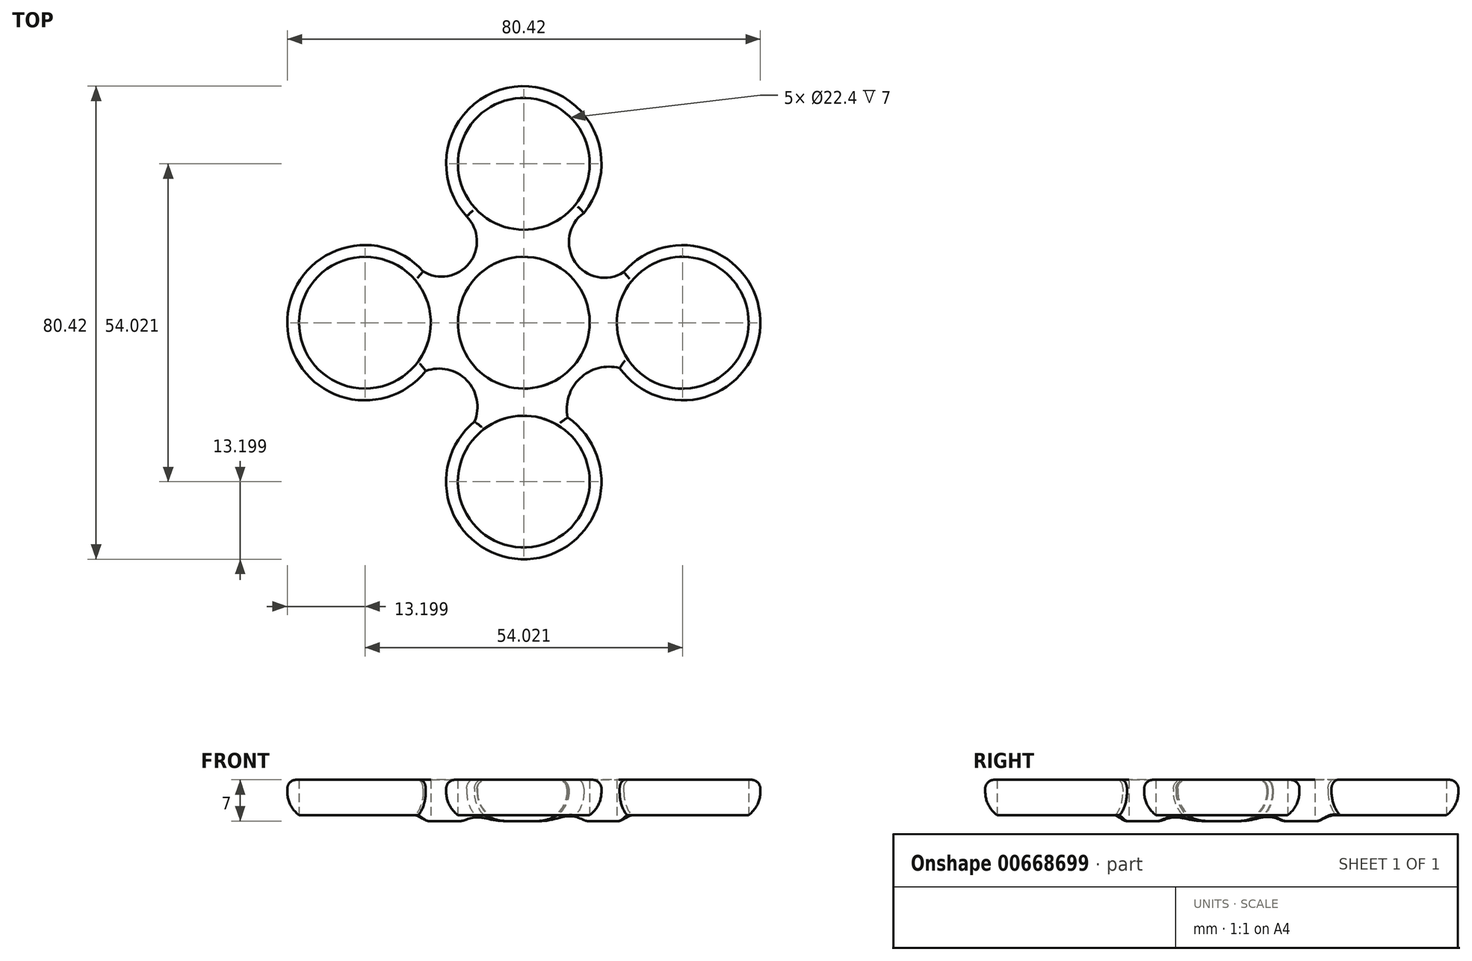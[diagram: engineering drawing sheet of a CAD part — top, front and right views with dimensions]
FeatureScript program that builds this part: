
annotation { "Feature Type Name" : "Feature", "Feature Type Description" : "" }
export const myFeature = defineFeature(function(context is Context, id is Id, definition is map)
    precondition{}
    {
        {
            var Q0;
            Q0=qCreatedBy(makeId("Top.planeOp"),FACE);
            var sketch = newSketch(context, id + "F0", { "sketchPlane" : qUnion([Q0])});
            skCircle(sketch, "E0", {"center": v(0, 0) * mm, "radius": 11.2 * mm});
            skCircle(sketch, "E1", {"center": v(0, 27.01) * mm, "radius": 11.2 * mm});
            skArc(sketch, "E2", {"start": v(8.69, 17.07) * mm, "mid": v(0.57, 40.2) * mm, "end": v(-9.5, 17.85) * mm});
            skCircle(sketch, "E3.1.0", {"center": v(-27.01, 0) * mm, "radius": 11.2 * mm});
            skArc(sketch, "E3.1.1", {"start": v(-17.1, 8.73) * mm, "mid": v(-40.2, -0.34) * mm, "end": v(-16.68, -8.21) * mm});
            skCircle(sketch, "E3.2.0", {"center": v(0, -27.01) * mm, "radius": 11.2 * mm});
            skArc(sketch, "E3.2.1", {"start": v(-8.38, -16.81) * mm, "mid": v(0.58, -40.2) * mm, "end": v(7.46, -16.12) * mm});
            skCircle(sketch, "E3.3.0", {"center": v(27.01, 0) * mm, "radius": 11.2 * mm});
            skArc(sketch, "E3.3.1", {"start": v(16.3, -7.7) * mm, "mid": v(40.2, -0.56) * mm, "end": v(17, 8.6) * mm});
            skArc(sketch, "E4", {"start": v(10.22, 18.65) * mm, "mid": v(8.7, 10.33) * mm, "end": v(17, 8.6) * mm});
            skArc(sketch, "E5", {"start": v(16.3, -7.7) * mm, "mid": v(9.54, -9.46) * mm, "end": v(7.46, -16.12) * mm});
            skArc(sketch, "E6", {"start": v(-8.38, -16.81) * mm, "mid": v(-9.7, -9.79) * mm, "end": v(-16.68, -8.21) * mm});
            skArc(sketch, "E7", {"start": v(-17.1, 8.73) * mm, "mid": v(-9.27, 10.11) * mm, "end": v(-9.7, 18.06) * mm});
            skPoint(sketch, "E7.endSnap0", {"position": v(-9.7, -9.79) * mm});
            skSolve(sketch);
        }
        {
            var Q0;
            Q0=makeQuery(id+"F0.imprint","IMPRINT",FACE,{"disambiguationData":[TD([[makeQuery(id+"F0.imprint","IMPRINT",EDGE,{"derivedFrom":sQuery(id+"F0.wireOp",EDGE,"E0")}),-1.0]])]});
            extrude(context, id + "F1", {"entities" : qUnion([Q0]), "depth" : 7 * mm, "offsetDistance" : 25 * mm});
        }
        {
            var Q0;
            Q0=makeQuery(id+"F1.opExtrude","CAP_EDGE",EDGE,{"disambiguationData":[OSD([sQuery(id+"F0.wireOp",EDGE,"E5")])],"isStart":false});
            var Q1;
            Q1=makeQuery(id+"F1.opExtrude","CAP_EDGE",EDGE,{"disambiguationData":[OSD([sQuery(id+"F0.wireOp",EDGE,"E3.3.1")])],"isStart":false});
            var Q2;
            Q2=makeQuery(id+"F1.opExtrude","CAP_EDGE",EDGE,{"disambiguationData":[OSD([sQuery(id+"F0.wireOp",EDGE,"E4")])],"isStart":false});
            var Q3;
            Q3=makeQuery(id+"F1.opExtrude","CAP_EDGE",EDGE,{"disambiguationData":[OSD([sQuery(id+"F0.wireOp",EDGE,"E2")])],"isStart":false});
            var Q4;
            Q4=makeQuery(id+"F1.opExtrude","CAP_EDGE",EDGE,{"disambiguationData":[OSD([sQuery(id+"F0.wireOp",EDGE,"E7")])],"isStart":false});
            var Q5;
            Q5=makeQuery(id+"F1.opExtrude","CAP_EDGE",EDGE,{"disambiguationData":[OSD([sQuery(id+"F0.wireOp",EDGE,"E3.1.1")])],"isStart":false});
            var Q6;
            Q6=makeQuery(id+"F1.opExtrude","CAP_EDGE",EDGE,{"disambiguationData":[OSD([sQuery(id+"F0.wireOp",EDGE,"E6")])],"isStart":false});
            var Q7;
            Q7=makeQuery(id+"F1.opExtrude","CAP_EDGE",EDGE,{"disambiguationData":[OSD([sQuery(id+"F0.wireOp",EDGE,"E3.2.1")])],"isStart":false});
            fillet(context, id + "F2", {"entities" : qUnion([Q0, Q1, Q2, Q3, Q4, Q5, Q6, Q7]), "radius" : 1.5 * mm, "tangentPropagation" : true, "allowEdgeOverflow" : false});
        }
        {
            var Q0;
            Q0=makeQuery(id+"F1.opExtrude","CAP_EDGE",EDGE,{"disambiguationData":[OSD([sQuery(id+"F0.wireOp",EDGE,"E3.2.1")])],"isStart":true});
            var Q1;
            Q1=makeQuery(id+"F1.opExtrude","CAP_EDGE",EDGE,{"disambiguationData":[OSD([sQuery(id+"F0.wireOp",EDGE,"E5")])],"isStart":true});
            var Q2;
            Q2=makeQuery(id+"F1.opExtrude","CAP_EDGE",EDGE,{"disambiguationData":[OSD([sQuery(id+"F0.wireOp",EDGE,"E3.3.1")])],"isStart":true});
            var Q3;
            Q3=makeQuery(id+"F1.opExtrude","CAP_EDGE",EDGE,{"disambiguationData":[OSD([sQuery(id+"F0.wireOp",EDGE,"E4")])],"isStart":true});
            var Q4;
            Q4=makeQuery(id+"F1.opExtrude","CAP_EDGE",EDGE,{"disambiguationData":[OSD([sQuery(id+"F0.wireOp",EDGE,"E2")])],"isStart":true});
            var Q5;
            Q5=makeQuery(id+"F1.opExtrude","CAP_EDGE",EDGE,{"disambiguationData":[OSD([sQuery(id+"F0.wireOp",EDGE,"E7")])],"isStart":true});
            var Q6;
            Q6=makeQuery(id+"F1.opExtrude","CAP_EDGE",EDGE,{"disambiguationData":[OSD([sQuery(id+"F0.wireOp",EDGE,"E6")])],"isStart":true});
            var Q7;
            Q7=makeQuery(id+"F1.opExtrude","CAP_EDGE",EDGE,{"disambiguationData":[OSD([sQuery(id+"F0.wireOp",EDGE,"E3.1.1")])],"isStart":true});
            fillet(context, id + "F3", {"entities" : qUnion([Q0, Q1, Q2, Q3, Q4, Q5, Q6, Q7]), "radius" : 5 * mm, "tangentPropagation" : true, "allowEdgeOverflow" : false});
        }
    });
